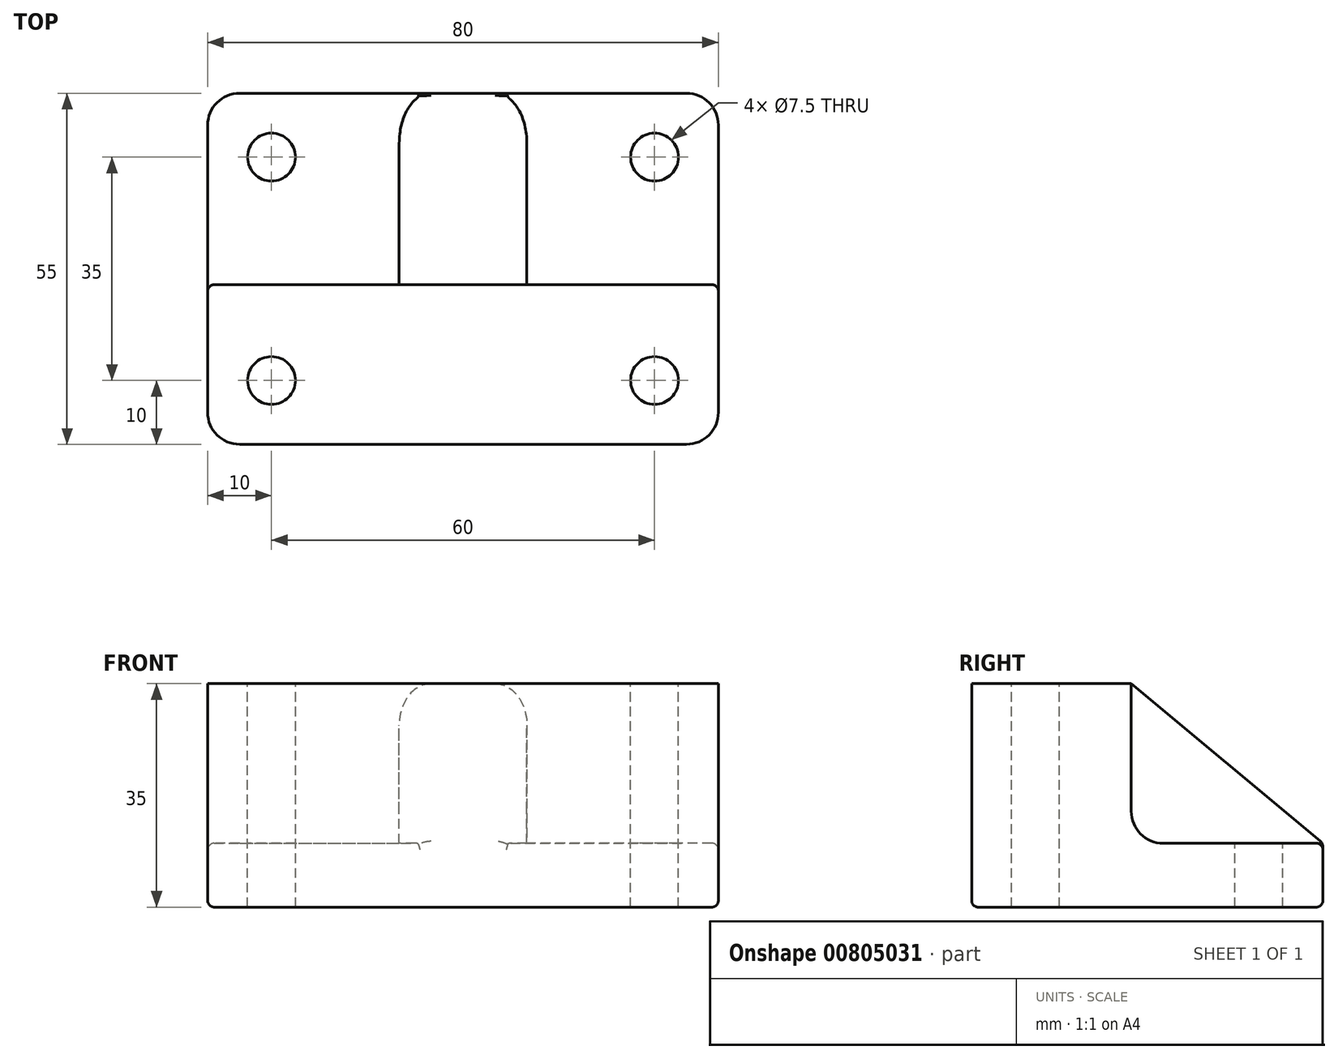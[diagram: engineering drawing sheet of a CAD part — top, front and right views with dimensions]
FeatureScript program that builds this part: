
annotation { "Feature Type Name" : "Feature", "Feature Type Description" : "" }
export const myFeature = defineFeature(function(context is Context, id is Id, definition is map)
    precondition{}
    {
        {
            var Q0;
            Q0=qCreatedBy(makeId("Top.planeOp"),FACE);
            var sketch = newSketch(context, id + "F0", { "sketchPlane" : qUnion([Q0])});
            skLineSegment(sketch, "E0.bottom", {"start": v(-40, 27.5) * mm, "end": v(40, 27.5) * mm});
            skLineSegment(sketch, "E0.top", {"start": v(-40, -27.5) * mm, "end": v(40, -27.5) * mm});
            skLineSegment(sketch, "E0.left", {"start": v(-40, 27.5) * mm, "end": v(-40, -27.5) * mm});
            skLineSegment(sketch, "E0.right", {"start": v(40, 27.5) * mm, "end": v(40, -27.5) * mm});
            skPoint(sketch, "E0.middle", {"position": v(0, 0) * mm});
            skSolve(sketch);
        }
        {
            var Q0;
            Q0 = qSketchRegion(id + "F0", true);
            extrude(context, id + "F1", {"entities" : qUnion([Q0]), "depth" : 35 * mm, "offsetDistance" : 25 * mm});
        }
        {
            var Q0;
            Q0=makeQuery(id+"F1.opExtrude","CAP_FACE",FACE,{"disambiguationData":[OSD([sQuery(id+"F0.wireOp",EDGE,"E0.bottom"),sQuery(id+"F0.wireOp",EDGE,"E0.top"),sQuery(id+"F0.wireOp",EDGE,"E0.left"),sQuery(id+"F0.wireOp",EDGE,"E0.right")])],"isStart":false});
            var sketch = newSketch(context, id + "F2", { "sketchPlane" : qUnion([Q0])});
            skLineSegment(sketch, "E1.bottom", {"start": v(-40, 27.5) * mm, "end": v(-10, 27.5) * mm});
            skLineSegment(sketch, "E1.top", {"start": v(-40, -2.5) * mm, "end": v(-10, -2.5) * mm});
            skLineSegment(sketch, "E1.left", {"start": v(-40, 27.5) * mm, "end": v(-40, -2.5) * mm});
            skLineSegment(sketch, "E1.right", {"start": v(-10, 27.5) * mm, "end": v(-10, -2.5) * mm});
            skLineSegment(sketch, "E2.bottom", {"start": v(40, 27.5) * mm, "end": v(10, 27.5) * mm});
            skLineSegment(sketch, "E2.top", {"start": v(40, -2.5) * mm, "end": v(10, -2.5) * mm});
            skLineSegment(sketch, "E2.left", {"start": v(40, 27.5) * mm, "end": v(40, -2.5) * mm});
            skLineSegment(sketch, "E2.right", {"start": v(10, 27.5) * mm, "end": v(10, -2.5) * mm});
            skLineSegment(sketch, "E3", {"start": v(0, 0) * mm, "end": v(0, 39.84) * mm, "construction": true});
            skSolve(sketch);
        }
        {
            var Q0;
            Q0 = qSketchRegion(id + "F2", true);
            extrude(context, id + "F3", {"entities" : qUnion([Q0]), "operationType" : NewBodyOperationType.REMOVE, "oppositeDirection" : true, "depth" : 25 * mm, "offsetDistance" : 25 * mm});
        }
        {
            var Q0;
            Q0=makeQuery(id+"F1.opExtrude","CAP_EDGE",EDGE,{"disambiguationData":[OSD([sQuery(id+"F0.wireOp",EDGE,"E0.bottom")])],"isStart":false});
            chamfer(context, id + "F4", {"entities" : qUnion([Q0]), "chamferType" : ChamferType.TWO_OFFSETS, "width1" : 25 * mm, "oppositeDirection" : false, "width2" : 30 * mm, "tangentPropagation" : true});
        }
        {
            var Q0;
            Q0=makeQuery(id+"F1.opExtrude","SWEPT_EDGE",EDGE,{"disambiguationData":[OSD([sQuery(id+"F0.wireOp",EDGE,"E0.top"),sQuery(id+"F0.wireOp",EDGE,"E0.left")])]});
            var Q1;
            Q1=makeQuery(id+"F3.boolean.opBoolean","COPY",EDGE,{"derivedFrom":makeQuery(id+"F3.opExtrude","SWEPT_EDGE",EDGE,{"disambiguationData":[OSD([sQuery(id+"F0.wireOp",EDGE,"E0.left"),sQuery(id+"F2.wireOp",EDGE,"E1.top"),sQuery(id+"F2.wireOp",EDGE,"E1.left")])]})});
            var Q2;
            Q2=makeQuery(id+"F1.opExtrude","SWEPT_EDGE",EDGE,{"disambiguationData":[OSD([sQuery(id+"F0.wireOp",EDGE,"E0.bottom"),sQuery(id+"F0.wireOp",EDGE,"E0.left")])]});
            var Q3;
            Q3=makeQuery(id+"F1.opExtrude","SWEPT_EDGE",EDGE,{"disambiguationData":[OSD([sQuery(id+"F0.wireOp",EDGE,"E0.top"),sQuery(id+"F0.wireOp",EDGE,"E0.right")])]});
            var Q4;
            Q4=makeQuery(id+"F3.boolean.opBoolean","COPY",EDGE,{"derivedFrom":makeQuery(id+"F3.opExtrude","SWEPT_EDGE",EDGE,{"disambiguationData":[OSD([sQuery(id+"F0.wireOp",EDGE,"E0.right"),sQuery(id+"F2.wireOp",EDGE,"E2.top"),sQuery(id+"F2.wireOp",EDGE,"E2.left")])]})});
            var Q5;
            Q5=makeQuery(id+"F1.opExtrude","SWEPT_EDGE",EDGE,{"disambiguationData":[OSD([sQuery(id+"F0.wireOp",EDGE,"E0.bottom"),sQuery(id+"F0.wireOp",EDGE,"E0.right")])]});
            fillet(context, id + "F5", {"entities" : qUnion([Q0, Q1, Q2, Q3, Q4, Q5]), "radius" : 5 * mm, "tangentPropagation" : true, "allowEdgeOverflow" : false});
        }
        {
            var Q0;
            Q0=makeQuery(id+"F3.boolean.opBoolean","COPY",EDGE,{"derivedFrom":makeQuery(id+"F3.opExtrude","CAP_EDGE",EDGE,{"disambiguationData":[OSD([sQuery(id+"F2.wireOp",EDGE,"E2.top")])],"isStart":false})});
            var Q1;
            Q1=makeQuery(id+"F3.boolean.opBoolean","COPY",EDGE,{"derivedFrom":makeQuery(id+"F3.opExtrude","CAP_EDGE",EDGE,{"disambiguationData":[OSD([sQuery(id+"F2.wireOp",EDGE,"E1.top")])],"isStart":false})});
            fillet(context, id + "F6", {"entities" : qUnion([Q0, Q1]), "radius" : 5 * mm, "tangentPropagation" : true, "allowEdgeOverflow" : false});
        }
        {
            var Q0;
            Q0=makeQuery(id+"F4.opChamfer","BLEND_EDGE",EDGE,{"blendedFrom":[makeQuery(id+"F1.opExtrude","CAP_EDGE",EDGE,{"disambiguationData":[OSD([sQuery(id+"F0.wireOp",EDGE,"E0.bottom")])],"isStart":false}),makeQuery(id+"F3.boolean.opBoolean","COPY",FACE,{"derivedFrom":makeQuery(id+"F3.opExtrude","SWEPT_FACE",FACE,{"disambiguationData":[OSD([sQuery(id+"F2.wireOp",EDGE,"E2.right")])]})})],"blendedInto":[makeQuery(id+"F3.boolean.opBoolean","COPY",FACE,{"derivedFrom":makeQuery(id+"F3.opExtrude","SWEPT_FACE",FACE,{"disambiguationData":[OSD([sQuery(id+"F2.wireOp",EDGE,"E2.right")])]})})]});
            var Q1;
            Q1=makeQuery(id+"F4.opChamfer","BLEND_EDGE",EDGE,{"blendedFrom":[makeQuery(id+"F1.opExtrude","CAP_EDGE",EDGE,{"disambiguationData":[OSD([sQuery(id+"F0.wireOp",EDGE,"E0.bottom")])],"isStart":false}),makeQuery(id+"F3.boolean.opBoolean","COPY",FACE,{"derivedFrom":makeQuery(id+"F3.opExtrude","SWEPT_FACE",FACE,{"disambiguationData":[OSD([sQuery(id+"F2.wireOp",EDGE,"E1.right")])]})})],"blendedInto":[makeQuery(id+"F3.boolean.opBoolean","COPY",FACE,{"derivedFrom":makeQuery(id+"F3.opExtrude","SWEPT_FACE",FACE,{"disambiguationData":[OSD([sQuery(id+"F2.wireOp",EDGE,"E1.right")])]})})]});
            fillet(context, id + "F7", {"entities" : qUnion([Q0, Q1]), "radius" : 5 * mm, "tangentPropagation" : true, "allowEdgeOverflow" : false});
        }
        {
            var Q0;
            Q0=makeQuery(id+"F1.opExtrude","CAP_FACE",FACE,{"disambiguationData":[OSD([sQuery(id+"F0.wireOp",EDGE,"E0.bottom"),sQuery(id+"F0.wireOp",EDGE,"E0.top"),sQuery(id+"F0.wireOp",EDGE,"E0.left"),sQuery(id+"F0.wireOp",EDGE,"E0.right")])],"isStart":false});
            var sketch = newSketch(context, id + "F8", { "sketchPlane" : qUnion([Q0])});
            skLineSegment(sketch, "E4", {"start": v(-40, -17.5) * mm, "end": v(40, -17.5) * mm, "construction": true});
            skLineSegment(sketch, "E5.bottom", {"start": v(-30, -17.5) * mm, "end": v(30, -17.5) * mm, "construction": true});
            skLineSegment(sketch, "E5.top", {"start": v(-30, 17.5) * mm, "end": v(30, 17.5) * mm, "construction": true});
            skLineSegment(sketch, "E5.left", {"start": v(-30, -17.5) * mm, "end": v(-30, 17.5) * mm, "construction": true});
            skLineSegment(sketch, "E5.right", {"start": v(30, -17.5) * mm, "end": v(30, 17.5) * mm, "construction": true});
            skLineSegment(sketch, "E6", {"start": v(0, 1.07) * mm, "end": v(0, 17.5) * mm, "construction": true});
            skSolve(sketch);
        }
        {
            var Q0;
            Q0=sQuery(id+"F8.wireOp",VERTEX,"E5.bottom.start");
            var Q1;
            Q1=sQuery(id+"F8.wireOp",VERTEX,"E5.bottom.end");
            var Q2;
            Q2=sQuery(id+"F8.wireOp",VERTEX,"E5.top.end");
            var Q3;
            Q3=sQuery(id+"F8.wireOp",VERTEX,"E5.top.start");
            var Q4;
            Q4=makeQuery(id+"F1.opExtrude","SWEPT_BODY",BODY,{"disambiguationData":[OSD([sQuery(id+"F0.wireOp",EDGE,"E0.bottom"),sQuery(id+"F0.wireOp",EDGE,"E0.top"),sQuery(id+"F0.wireOp",EDGE,"E0.left"),sQuery(id+"F0.wireOp",EDGE,"E0.right")])]});
            hole(context, id + "F9", {"style" : HoleStyle.SIMPLE, "endStyle" : HoleEndStyle.THROUGH, "holeDiameter" : 7.5 * mm, "majorDiameter" : 5 * mm, "isTappedThrough" : true, "tappedDepth" : 12 * mm, "tapClearance" : 3, "locations" : qUnion([Q0, Q1, Q2, Q3]), "scope" : qUnion([Q4])});
        }
        {
            var Q0;
            {var subQ0=sQuery(id+"F0.wireOp",EDGE,"E0.right");Q0=makeQuery(id+"F5.opFillet","BLEND_EDGE",EDGE,{"blendedFrom":[makeQuery(id+"F3.boolean.opBoolean","COPY",EDGE,{"derivedFrom":makeQuery(id+"F3.opExtrude","SWEPT_EDGE",EDGE,{"disambiguationData":[OSD([subQ0,sQuery(id+"F2.wireOp",EDGE,"E2.top"),sQuery(id+"F2.wireOp",EDGE,"E2.left")])]})}),makeQuery(id+"F1.opExtrude","CAP_FACE",FACE,{"disambiguationData":[OSD([sQuery(id+"F0.wireOp",EDGE,"E0.bottom"),sQuery(id+"F0.wireOp",EDGE,"E0.top"),sQuery(id+"F0.wireOp",EDGE,"E0.left"),subQ0])],"isStart":false})],"blendedInto":[makeQuery(id+"F1.opExtrude","CAP_FACE",FACE,{"disambiguationData":[OSD([sQuery(id+"F0.wireOp",EDGE,"E0.bottom"),sQuery(id+"F0.wireOp",EDGE,"E0.top"),sQuery(id+"F0.wireOp",EDGE,"E0.left"),subQ0])],"isStart":false})]});}
            var Q1;
            {var subQ0=sQuery(id+"F0.wireOp",EDGE,"E0.bottom");Q1=makeQuery(id+"F7.opFillet","MERGE",EDGE,{"derivedFrom":[makeQuery(id+"F4.opChamfer","BLEND_EDGE",EDGE,{"blendedFrom":[makeQuery(id+"F1.opExtrude","CAP_EDGE",EDGE,{"disambiguationData":[OSD([subQ0])],"isStart":false}),makeQuery(id+"F1.opExtrude","SWEPT_FACE",FACE,{"disambiguationData":[OSD([subQ0])]})],"blendedInto":[makeQuery(id+"F1.opExtrude","SWEPT_FACE",FACE,{"disambiguationData":[OSD([subQ0])]})]}),makeQuery(id+"F3.boolean.opBoolean","COPY",EDGE,{"derivedFrom":makeQuery(id+"F3.opExtrude","CAP_EDGE",EDGE,{"disambiguationData":[OSD([sQuery(id+"F2.wireOp",EDGE,"E2.bottom")])],"isStart":false})})]});}
            var Q2;
            {var subQ0=sQuery(id+"F0.wireOp",EDGE,"E0.bottom");Q2=makeQuery(id+"F7.opFillet","MERGE",EDGE,{"derivedFrom":[makeQuery(id+"F4.opChamfer","BLEND_EDGE",EDGE,{"blendedFrom":[makeQuery(id+"F1.opExtrude","CAP_EDGE",EDGE,{"disambiguationData":[OSD([subQ0])],"isStart":false}),makeQuery(id+"F1.opExtrude","SWEPT_FACE",FACE,{"disambiguationData":[OSD([subQ0])]})],"blendedInto":[makeQuery(id+"F1.opExtrude","SWEPT_FACE",FACE,{"disambiguationData":[OSD([subQ0])]})]}),makeQuery(id+"F3.boolean.opBoolean","COPY",EDGE,{"derivedFrom":makeQuery(id+"F3.opExtrude","CAP_EDGE",EDGE,{"disambiguationData":[OSD([sQuery(id+"F2.wireOp",EDGE,"E1.bottom")])],"isStart":false})})]});}
            var Q3;
            Q3=makeQuery(id+"F1.opExtrude","CAP_EDGE",EDGE,{"disambiguationData":[OSD([sQuery(id+"F0.wireOp",EDGE,"E0.top")])],"isStart":true});
            var Q4;
            Q4=makeQuery(id+"F9.hole-1.boolean.opBoolean","COPY",FACE,{"derivedFrom":makeQuery(id+"F9.hole-1.opRevolve","SWEPT_FACE",FACE,{"disambiguationData":[OSD([sQuery(id+"F9.hole-1.sketch.wireOp",EDGE,"core_line_2")])]})});
            var Q5;
            Q5=makeQuery(id+"F9.hole-0.boolean.opBoolean","COPY",FACE,{"derivedFrom":makeQuery(id+"F9.hole-0.opRevolve","SWEPT_FACE",FACE,{"disambiguationData":[OSD([sQuery(id+"F9.hole-0.sketch.wireOp",EDGE,"core_line_2")])]})});
            var Q6;
            Q6=makeQuery(id+"F9.hole-3.boolean.opBoolean","COPY",FACE,{"derivedFrom":makeQuery(id+"F9.hole-3.opRevolve","SWEPT_FACE",FACE,{"disambiguationData":[OSD([sQuery(id+"F9.hole-3.sketch.wireOp",EDGE,"core_line_2")])]})});
            var Q7;
            Q7=makeQuery(id+"F9.hole-2.boolean.opBoolean","COPY",FACE,{"derivedFrom":makeQuery(id+"F9.hole-2.opRevolve","SWEPT_FACE",FACE,{"disambiguationData":[OSD([sQuery(id+"F9.hole-2.sketch.wireOp",EDGE,"core_line_2")])]})});
            fillet(context, id + "F10", {"entities" : qUnion([Q0, Q1, Q2, Q3, Q4, Q5, Q6, Q7]), "radius" : 1 * mm, "tangentPropagation" : true, "allowEdgeOverflow" : false});
        }
    });
